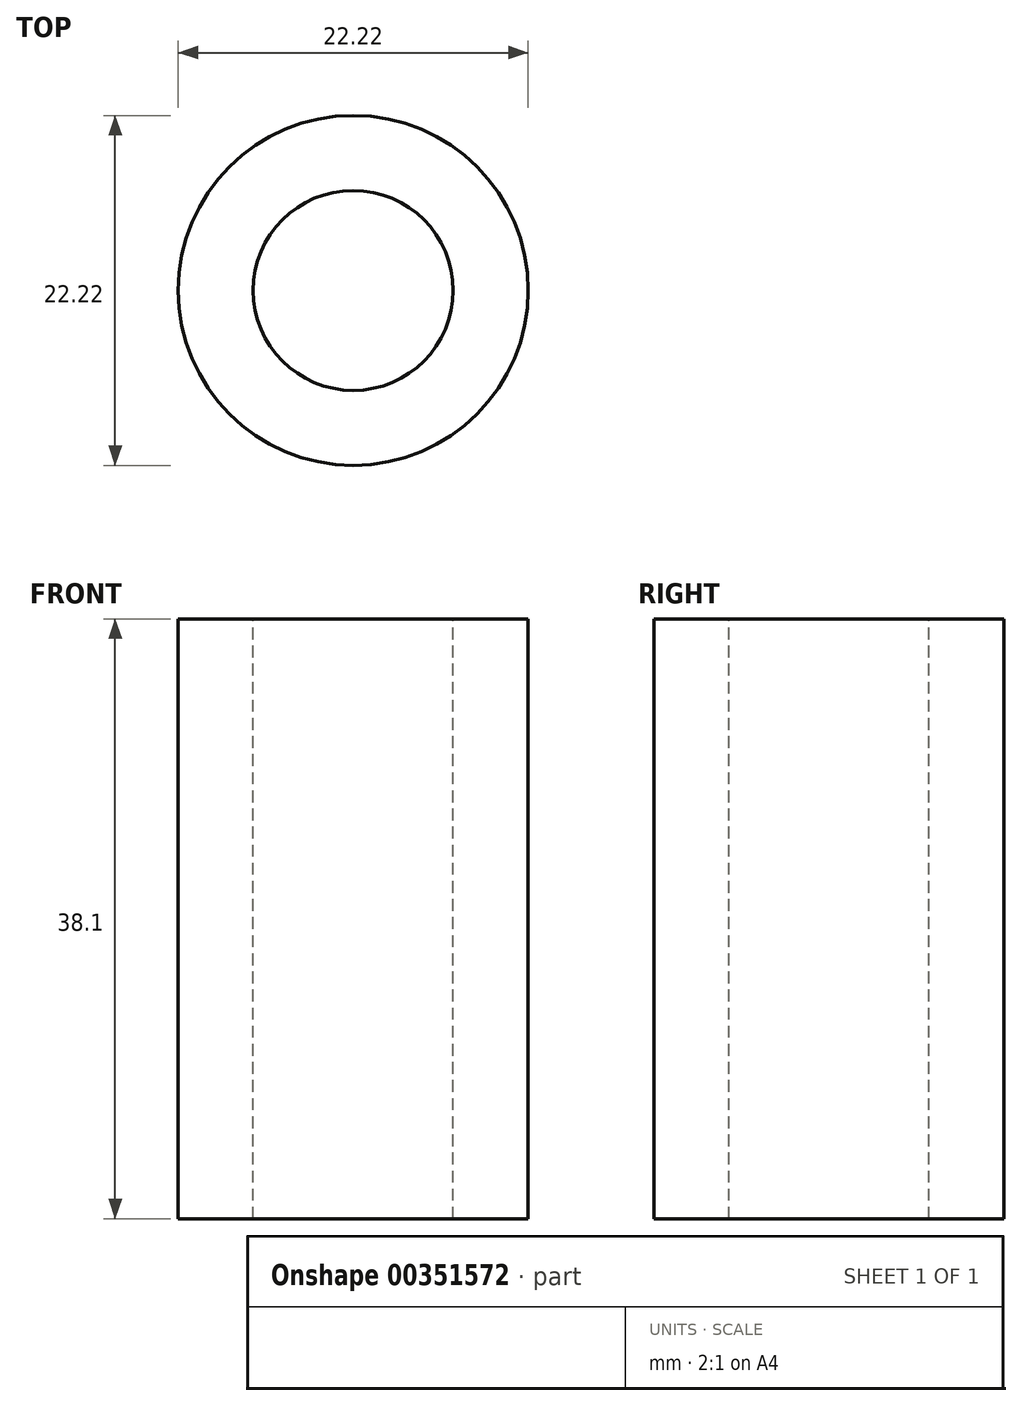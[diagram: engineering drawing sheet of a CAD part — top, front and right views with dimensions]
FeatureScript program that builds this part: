
annotation { "Feature Type Name" : "Feature", "Feature Type Description" : "" }
export const myFeature = defineFeature(function(context is Context, id is Id, definition is map)
    precondition{}
    {
        {
            var Q0;
            Q0=qCreatedBy(makeId("Top.planeOp"),FACE);
            var sketch = newSketch(context, id + "F0", { "sketchPlane" : qUnion([Q0])});
            skCircle(sketch, "E0", {"center": v(0, 0) * mm, "radius": 11.11 * mm});
            skSolve(sketch);
        }
        {
            var Q0;
            Q0=makeQuery(id+"F0.imprint","IMPRINT",FACE,{"disambiguationData":[TD([[makeQuery(id+"F0.imprint","IMPRINT",EDGE,{"derivedFrom":sQuery(id+"F0.wireOp",EDGE,"E0")}),1.0]])]});
            extrude(context, id + "F1", {"entities" : qUnion([Q0]), "depth" : 38.1 * mm, "symmetric" : true});
        }
        {
            var Q0;
            Q0=makeQuery(id+"F1.opExtrude","CAP_FACE",FACE,{"disambiguationData":[OSD([sQuery(id+"F0.wireOp",EDGE,"E0")])],"isStart":false});
            var sketch = newSketch(context, id + "F2", { "sketchPlane" : qUnion([Q0])});
            skCircle(sketch, "E1", {"center": v(0, 0) * mm, "radius": 6.35 * mm});
            skSolve(sketch);
        }
        {
            var Q0;
            Q0 = qSketchRegion(id + "F2", true);
            var Q1;
            Q1=makeQuery(id+"F1.opExtrude","CAP_FACE",FACE,{"disambiguationData":[OSD([sQuery(id+"F0.wireOp",EDGE,"E0")])],"isStart":true});
            extrude(context, id + "F3", {"entities" : qUnion([Q0]), "operationType" : NewBodyOperationType.REMOVE, "endBound" : BoundingType.UP_TO_SURFACE, "oppositeDirection" : true, "endBoundEntityFace" : qUnion([Q1]), "depth" : 25.4 * mm});
        }
    });
